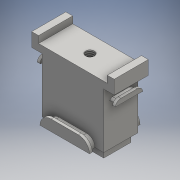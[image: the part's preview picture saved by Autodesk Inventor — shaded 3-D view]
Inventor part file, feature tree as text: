
AUTODESK INVENTOR PART (.ipt)
format: ipt  version: 2016 (Build 200138000, 138)  size: 255,488 bytes
history: native  units: mm
features: sketch x9, extrude x8, projected_geometry x7, plane x2, mirror x2, hole x1, fillet x1
ambient origin geometry x8: Origin, YZ Plane, XZ Plane, XY Plane, X Axis, Y Axis, Z Axis, Center Point
bodies: Solid1 (feature_tree)
feature tree (30):
  extrude  "Extrusion1"  Depth=19.9mm
  extrude  "Extrusion2"  Depth=1.25mm
  extrude  "Extrusion3"  Depth=1.25mm
  extrude  "Extrusion4"  Depth=30.0mm
  hole  "Hole1"  [1 undecoded]
  extrude  "Extrusion5"  Depth=2.5mm TaperAngle=0.0deg
  extrude  "Extrusion6"  Depth=8.0mm
  plane  "Work Plane1"
  plane  "Work Plane2"
  mirror  "Mirror1"
  extrude  "Extrusion7"  Depth=2.0mm TaperAngle=0.0deg
  extrude  "Extrusion8"  Depth=1.0mm TaperAngle=0.0deg
  fillet  "Fillet1"  Radius=4.0mm
  mirror  "Mirror2"
  sketch  "Sketch1"  dims[d0=9.9mm d1=19.9mm]
  sketch  "Sketch2"  dims[d2=3.0mm d3=0.0mm d5=1.25mm]
  projected_geometry  "Projected Loop1"
  sketch  "Sketch3"  dims[d6=1.25mm d7=1.25mm]
  projected_geometry  "Projected Loop2"
  sketch  "Sketch4"  dims[d8=20.0mm d9=0.0mm d10=30.0mm]
  projected_geometry  "Projected Loop3"
  sketch  "Sketch5"  dims[d11=5.0mm d12=0.0mm d13=25.0mm]
  sketch  "Sketch6"  dims[d14=25.000003mm d15=2.5mm d16=0.0mm]
  projected_geometry  "Projected Loop4"
  sketch  "Sketch7"  dims[d17=3.242mm d18=8.0mm d19=4.0mm d20=2.0mm d21=90.0deg d22=10.0mm d23=20.594885mm d24=8.0mm]
  projected_geometry  "Projected Loop5"
  sketch  "Sketch8"  dims[d28=3.0mm d29=2.0mm d30=0.0mm]
  projected_geometry  "Projected Loop6"
  sketch  "Sketch9"  dims[d33=1.0mm d35=1.0mm d36=0.0mm d37=4.0mm d38=90.0deg d40=15.0mm d41=2.0mm d42=0.0mm d44=1.0mm d45=1.0mm d46=90.0deg d47=1.0mm d48=0.0mm d49=0.25mm]
  projected_geometry  "Projected Loop7"
note: 1 required parameter value undecoded (feature->parameter linkage not recoverable at this tier; creation-order binding heuristic only, values carry confidence <= 0.55)
